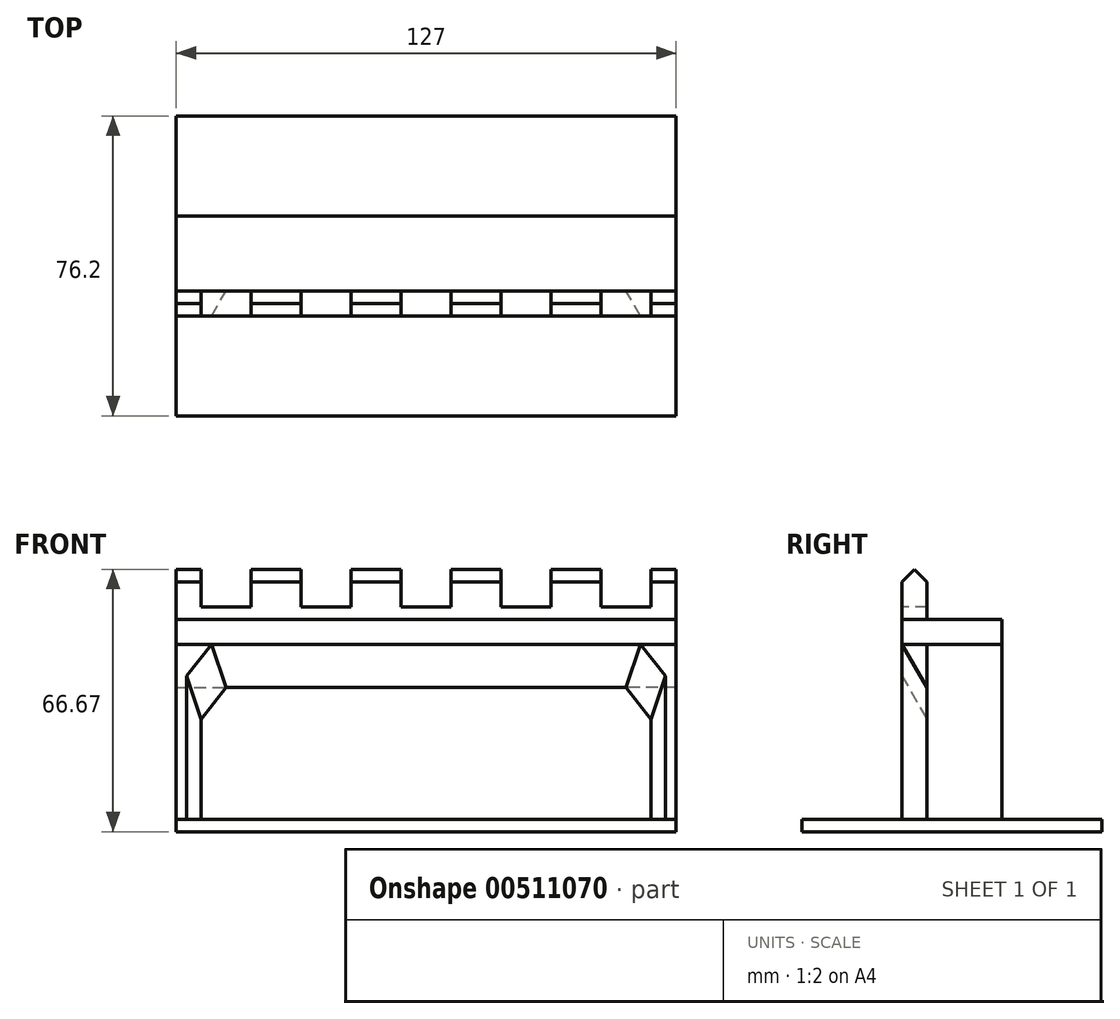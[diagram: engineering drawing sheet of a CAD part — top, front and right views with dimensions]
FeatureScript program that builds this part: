
annotation { "Feature Type Name" : "Feature", "Feature Type Description" : "" }
export const myFeature = defineFeature(function(context is Context, id is Id, definition is map)
    precondition{}
    {
        {
            var Q0;
            Q0=qCreatedBy(makeId("Top.planeOp"),FACE);
            var sketch = newSketch(context, id + "F0", { "sketchPlane" : qUnion([Q0])});
            skLineSegment(sketch, "E0.bottom", {"start": v(63.5, 38.1) * mm, "end": v(-63.5, 38.1) * mm});
            skLineSegment(sketch, "E0.top", {"start": v(63.5, -38.1) * mm, "end": v(-63.5, -38.1) * mm});
            skLineSegment(sketch, "E0.left", {"start": v(63.5, 38.1) * mm, "end": v(63.5, -38.1) * mm});
            skLineSegment(sketch, "E0.right", {"start": v(-63.5, 38.1) * mm, "end": v(-63.5, -38.1) * mm});
            skPoint(sketch, "E0.middle", {"position": v(0, 0) * mm});
            skSolve(sketch);
        }
        {
            var Q0;
            Q0 = qSketchRegion(id + "F0", true);
            extrude(context, id + "F1", {"entities" : qUnion([Q0]), "depth" : 3.17 * mm});
        }
        {
            var Q0;
            Q0=makeQuery(id+"F1.opExtrude","CAP_FACE",FACE,{"disambiguationData":[OSD([sQuery(id+"F0.wireOp",EDGE,"E0.bottom"),sQuery(id+"F0.wireOp",EDGE,"E0.top"),sQuery(id+"F0.wireOp",EDGE,"E0.left"),sQuery(id+"F0.wireOp",EDGE,"E0.right")])],"isStart":false});
            var sketch = newSketch(context, id + "F2", { "sketchPlane" : qUnion([Q0])});
            skLineSegment(sketch, "E1.bottom", {"start": v(-63.5, -6.35) * mm, "end": v(63.5, -6.35) * mm});
            skLineSegment(sketch, "E1.top", {"start": v(-63.5, 12.7) * mm, "end": v(63.5, 12.7) * mm});
            skLineSegment(sketch, "E1.left", {"start": v(-63.5, -6.35) * mm, "end": v(-63.5, 12.7) * mm});
            skLineSegment(sketch, "E1.right", {"start": v(63.5, -6.35) * mm, "end": v(63.5, 12.7) * mm});
            skSolve(sketch);
        }
        {
            var Q0;
            Q0 = qSketchRegion(id + "F2", true);
            extrude(context, id + "F3", {"entities" : qUnion([Q0]), "depth" : 44.45 * mm});
        }
        {
            var Q0;
            Q0=makeQuery(id+"F3.opExtrude","CAP_FACE",FACE,{"disambiguationData":[OSD([sQuery(id+"F2.wireOp",EDGE,"E1.bottom"),sQuery(id+"F2.wireOp",EDGE,"E1.top"),sQuery(id+"F2.wireOp",EDGE,"E1.left"),sQuery(id+"F2.wireOp",EDGE,"E1.right")])],"isStart":false});
            var sketch = newSketch(context, id + "F4", { "sketchPlane" : qUnion([Q0])});
            skLineSegment(sketch, "E2.bottom", {"start": v(-63.5, 12.7) * mm, "end": v(63.5, 12.7) * mm});
            skLineSegment(sketch, "E2.top", {"start": v(-63.5, -12.7) * mm, "end": v(63.5, -12.7) * mm});
            skLineSegment(sketch, "E2.left", {"start": v(-63.5, 12.7) * mm, "end": v(-63.5, -12.7) * mm});
            skLineSegment(sketch, "E2.right", {"start": v(63.5, 12.7) * mm, "end": v(63.5, -12.7) * mm});
            skSolve(sketch);
        }
        {
            var Q0;
            {var subQ0=sQuery(id+"F4.wireOp",EDGE,"E2.top");Q0=makeQuery(id+"F4.imprint","IMPRINT",FACE,{"disambiguationData":[TD([[makeQuery(id+"F4.imprint","IMPRINT",EDGE,{"derivedFrom":subQ0}),1.0]])]});}
            var Q1;
            {var subQ0=sQuery(id+"F4.wireOp",EDGE,"E2.bottom");Q1=makeQuery(id+"F4.imprint","IMPRINT",FACE,{"disambiguationData":[TD([[makeQuery(id+"F4.imprint","IMPRINT",EDGE,{"derivedFrom":subQ0}),-1.0]])]});}
            extrude(context, id + "F5", {"entities" : qUnion([Q0, Q1]), "depth" : 6.35 * mm});
        }
        {
            var Q0;
            Q0=makeQuery(id+"F5.opExtrude","CAP_FACE",FACE,{"disambiguationData":[OSD([sQuery(id+"F4.wireOp",EDGE,"E2.bottom"),sQuery(id+"F4.wireOp",EDGE,"E2.top"),sQuery(id+"F4.wireOp",EDGE,"E2.left"),sQuery(id+"F4.wireOp",EDGE,"E2.right")])],"isStart":false});
            var sketch = newSketch(context, id + "F6", { "sketchPlane" : qUnion([Q0])});
            skLineSegment(sketch, "E3.bottom", {"start": v(-63.5, -12.7) * mm, "end": v(63.5, -12.7) * mm});
            skLineSegment(sketch, "E3.top", {"start": v(-63.5, -6.35) * mm, "end": v(63.5, -6.35) * mm});
            skLineSegment(sketch, "E3.left", {"start": v(-63.5, -12.7) * mm, "end": v(-63.5, -6.35) * mm});
            skLineSegment(sketch, "E3.right", {"start": v(63.5, -12.7) * mm, "end": v(63.5, -6.35) * mm});
            skSolve(sketch);
        }
        {
            var Q0;
            Q0 = qSketchRegion(id + "F6", true);
            extrude(context, id + "F7", {"entities" : qUnion([Q0]), "depth" : 12.7 * mm});
        }
        {
            var Q0;
            Q0=makeQuery(id+"F7.opExtrude","SWEPT_FACE",FACE,{"disambiguationData":[OSD([sQuery(id+"F6.wireOp",EDGE,"E3.right")])]});
            var sketch = newSketch(context, id + "F8", { "sketchPlane" : qUnion([Q0])});
            skLineSegment(sketch, "E4.bottom", {"start": v(-12.7, 66.67) * mm, "end": v(-6.35, 66.67) * mm});
            skLineSegment(sketch, "E4.top", {"start": v(-12.7, 63.5) * mm, "end": v(-6.35, 63.5) * mm, "construction": true});
            skLineSegment(sketch, "E4.left", {"start": v(-12.7, 66.67) * mm, "end": v(-12.7, 63.5) * mm});
            skLineSegment(sketch, "E4.right", {"start": v(-6.35, 66.67) * mm, "end": v(-6.35, 63.5) * mm});
            skLineSegment(sketch, "E5", {"start": v(-12.7, 63.5) * mm, "end": v(-9.52, 66.67) * mm});
            skLineSegment(sketch, "E6", {"start": v(-9.53, 66.67) * mm, "end": v(-6.35, 63.5) * mm});
            skSolve(sketch);
        }
        {
            var Q0;
            Q0 = qSketchRegion(id + "F8", true);
            var Q1;
            Q1=makeQuery(id+"F7.opExtrude","SWEPT_FACE",FACE,{"disambiguationData":[OSD([sQuery(id+"F6.wireOp",EDGE,"E3.left")])]});
            extrude(context, id + "F9", {"entities" : qUnion([Q0]), "operationType" : NewBodyOperationType.REMOVE, "endBound" : BoundingType.UP_TO_SURFACE, "oppositeDirection" : true, "endBoundEntityFace" : qUnion([Q1]), "depth" : 25.4 * mm});
        }
        {
            var Q0;
            Q0=makeQuery(id+"F7.opExtrude","SWEPT_FACE",FACE,{"disambiguationData":[OSD([sQuery(id+"F6.wireOp",EDGE,"E3.bottom")])]});
            var sketch = newSketch(context, id + "F10", { "sketchPlane" : qUnion([Q0])});
            skLineSegment(sketch, "E7.bottom", {"start": v(-57.15, 66.67) * mm, "end": v(-44.45, 66.67) * mm});
            skLineSegment(sketch, "E7.top", {"start": v(-57.15, 57.15) * mm, "end": v(-44.45, 57.15) * mm});
            skLineSegment(sketch, "E7.left", {"start": v(-57.15, 66.67) * mm, "end": v(-57.15, 57.15) * mm});
            skLineSegment(sketch, "E7.right", {"start": v(-44.45, 66.67) * mm, "end": v(-44.45, 57.15) * mm});
            skLineSegment(sketch, "E8", {"start": v(-44.45, 61.91) * mm, "end": v(-31.75, 61.91) * mm, "construction": true});
            skLineSegment(sketch, "E9.bottom", {"start": v(-31.75, 66.67) * mm, "end": v(-19.05, 66.67) * mm});
            skLineSegment(sketch, "E9.top", {"start": v(-31.75, 57.15) * mm, "end": v(-19.05, 57.15) * mm});
            skLineSegment(sketch, "E9.left", {"start": v(-31.75, 66.67) * mm, "end": v(-31.75, 57.15) * mm});
            skLineSegment(sketch, "E9.right", {"start": v(-19.05, 66.67) * mm, "end": v(-19.05, 57.15) * mm});
            skLineSegment(sketch, "E10", {"start": v(-19.05, 61.91) * mm, "end": v(-6.35, 61.91) * mm, "construction": true});
            skLineSegment(sketch, "E11.bottom", {"start": v(-6.35, 66.67) * mm, "end": v(0, 66.67) * mm});
            skLineSegment(sketch, "E11.top", {"start": v(-6.35, 57.15) * mm, "end": v(0, 57.15) * mm});
            skLineSegment(sketch, "E11.left", {"start": v(-6.35, 66.67) * mm, "end": v(-6.35, 57.15) * mm});
            skLineSegment(sketch, "E12.MirrorCS", {"start": v(6.35, 66.67) * mm, "end": v(6.35, 57.15) * mm});
            skLineSegment(sketch, "E13.MirrorCS", {"start": v(19.05, 61.91) * mm, "end": v(6.35, 61.91) * mm, "construction": true});
            skLineSegment(sketch, "E14.MirrorCS", {"start": v(6.35, 66.67) * mm, "end": v(0, 66.67) * mm});
            skLineSegment(sketch, "E15.MirrorCS", {"start": v(19.05, 66.67) * mm, "end": v(19.05, 57.15) * mm});
            skLineSegment(sketch, "E16.MirrorCS", {"start": v(44.45, 66.67) * mm, "end": v(44.45, 57.15) * mm});
            skLineSegment(sketch, "E17.MirrorCS", {"start": v(6.35, 57.15) * mm, "end": v(0, 57.15) * mm});
            skLineSegment(sketch, "E18.MirrorCS", {"start": v(57.15, 66.67) * mm, "end": v(57.15, 57.15) * mm});
            skLineSegment(sketch, "E19.MirrorCS", {"start": v(57.15, 57.15) * mm, "end": v(44.45, 57.15) * mm});
            skLineSegment(sketch, "E20.MirrorCS", {"start": v(57.15, 66.67) * mm, "end": v(44.45, 66.67) * mm});
            skLineSegment(sketch, "E21.MirrorCS", {"start": v(31.75, 57.15) * mm, "end": v(19.05, 57.15) * mm});
            skLineSegment(sketch, "E22.MirrorCS", {"start": v(31.75, 66.67) * mm, "end": v(19.05, 66.67) * mm});
            skLineSegment(sketch, "E23.MirrorCS", {"start": v(44.45, 61.91) * mm, "end": v(31.75, 61.91) * mm, "construction": true});
            skLineSegment(sketch, "E24.MirrorCS", {"start": v(31.75, 66.67) * mm, "end": v(31.75, 57.15) * mm});
            skSolve(sketch);
        }
        {
            var Q0;
            Q0 = qSketchRegion(id + "F10", true);
            var Q1;
            Q1=makeQuery(id+"F7.opExtrude","SWEPT_FACE",FACE,{"disambiguationData":[OSD([sQuery(id+"F6.wireOp",EDGE,"E3.top")])]});
            extrude(context, id + "F11", {"entities" : qUnion([Q0]), "operationType" : NewBodyOperationType.REMOVE, "endBound" : BoundingType.UP_TO_SURFACE, "oppositeDirection" : true, "endBoundEntityFace" : qUnion([Q1]), "depth" : 25.4 * mm});
        }
        {
            var Q0;
            Q0=makeQuery(id+"F3.opExtrude","SWEPT_FACE",FACE,{"disambiguationData":[OSD([sQuery(id+"F2.wireOp",EDGE,"E1.right")])]});
            var sketch = newSketch(context, id + "F12", { "sketchPlane" : qUnion([Q0])});
            skLineSegment(sketch, "E25", {"start": v(-12.7, 47.62) * mm, "end": v(-6.35, 36.63) * mm});
            skLineSegment(sketch, "E26", {"start": v(-6.35, 47.62) * mm, "end": v(-6.35, 36.63) * mm});
            skLineSegment(sketch, "E27", {"start": v(-6.35, 47.62) * mm, "end": v(-12.7, 47.62) * mm});
            skSolve(sketch);
        }
        {
            var Q0;
            Q0 = qSketchRegion(id + "F12", true);
            var Q1;
            Q1=makeQuery(id+"F3.opExtrude","SWEPT_FACE",FACE,{"disambiguationData":[OSD([sQuery(id+"F2.wireOp",EDGE,"E1.left")])]});
            extrude(context, id + "F13", {"entities" : qUnion([Q0]), "endBound" : BoundingType.UP_TO_SURFACE, "oppositeDirection" : true, "endBoundEntityFace" : qUnion([Q1]), "depth" : 25.4 * mm});
        }
        {
            var Q0;
            Q0=makeQuery(id+"F1.opExtrude","CAP_FACE",FACE,{"disambiguationData":[OSD([sQuery(id+"F0.wireOp",EDGE,"E0.bottom"),sQuery(id+"F0.wireOp",EDGE,"E0.top"),sQuery(id+"F0.wireOp",EDGE,"E0.left"),sQuery(id+"F0.wireOp",EDGE,"E0.right")])],"isStart":false});
            var sketch = newSketch(context, id + "F14", { "sketchPlane" : qUnion([Q0])});
            skLineSegment(sketch, "E28.bottom", {"start": v(50.8, -6.35) * mm, "end": v(63.5, -6.35) * mm});
            skLineSegment(sketch, "E28.top", {"start": v(54.47, -12.7) * mm, "end": v(63.5, -12.7) * mm});
            skLineSegment(sketch, "E28.left", {"start": v(50.8, -6.35) * mm, "end": v(54.47, -12.7) * mm});
            skLineSegment(sketch, "E28.right", {"start": v(76.2, -6.35) * mm, "end": v(72.53, -12.7) * mm, "construction": true});
            skLineSegment(sketch, "E29", {"start": v(63.5, -6.35) * mm, "end": v(63.5, -12.7) * mm});
            skLineSegment(sketch, "E30", {"start": v(63.5, -12.7) * mm, "end": v(72.53, -12.7) * mm, "construction": true});
            skLineSegment(sketch, "E31", {"start": v(63.5, -6.35) * mm, "end": v(76.2, -6.35) * mm, "construction": true});
            skSolve(sketch);
        }
        {
            var Q0;
            Q0 = qSketchRegion(id + "F14", true);
            var Q1;
            Q1=makeQuery(id+"F13.opExtrude","SWEPT_FACE",FACE,{"disambiguationData":[OSD([sQuery(id+"F12.wireOp",EDGE,"E25")])]});
            extrude(context, id + "F15", {"entities" : qUnion([Q0]), "endBound" : BoundingType.UP_TO_SURFACE, "endBoundEntityFace" : qUnion([Q1]), "depth" : 25.4 * mm});
        }
        {
            var Q0;
            Q0=makeQuery(id+"F1.opExtrude","CAP_FACE",FACE,{"disambiguationData":[OSD([sQuery(id+"F0.wireOp",EDGE,"E0.bottom"),sQuery(id+"F0.wireOp",EDGE,"E0.top"),sQuery(id+"F0.wireOp",EDGE,"E0.left"),sQuery(id+"F0.wireOp",EDGE,"E0.right")])],"isStart":false});
            var sketch = newSketch(context, id + "F16", { "sketchPlane" : qUnion([Q0])});
            skLineSegment(sketch, "E32.bottom", {"start": v(57.15, -6.35) * mm, "end": v(63.5, -6.35) * mm, "construction": true});
            skLineSegment(sketch, "E32.top", {"start": v(60.82, -12.7) * mm, "end": v(63.5, -12.7) * mm, "construction": true});
            skLineSegment(sketch, "E32.left", {"start": v(57.15, -6.35) * mm, "end": v(60.82, -12.7) * mm});
            skLineSegment(sketch, "E32.right", {"start": v(69.85, -6.35) * mm, "end": v(66.18, -12.7) * mm, "construction": true});
            skLineSegment(sketch, "E33", {"start": v(63.5, -6.35) * mm, "end": v(63.5, -12.7) * mm});
            skLineSegment(sketch, "E34", {"start": v(63.5, -12.7) * mm, "end": v(66.18, -12.7) * mm, "construction": true});
            skLineSegment(sketch, "E35", {"start": v(63.5, -6.35) * mm, "end": v(69.85, -6.35) * mm, "construction": true});
            skLineSegment(sketch, "E36", {"start": v(60.82, -12.7) * mm, "end": v(54.47, -12.7) * mm});
            skLineSegment(sketch, "E37", {"start": v(54.47, -12.7) * mm, "end": v(50.8, -6.35) * mm});
            skLineSegment(sketch, "E38", {"start": v(50.8, -6.35) * mm, "end": v(57.15, -6.35) * mm});
            skSolve(sketch);
        }
        {
            var Q0;
            Q0 = qSketchRegion(id + "F16", true);
            extrude(context, id + "F17", {"entities" : qUnion([Q0]), "operationType" : NewBodyOperationType.REMOVE, "depth" : 25.4 * mm});
        }
        {
            var Q0;
            Q0=makeQuery(id+"F15.opExtrude","CAP_VERTEX",VERTEX,{"disambiguationData":[OSD([sQuery(id+"F12.wireOp",EDGE,"E25"),sQuery(id+"F14.wireOp",EDGE,"E28.top"),sQuery(id+"F14.wireOp",EDGE,"E28.left")])],"isStart":false});
            var Q1;
            Q1=makeQuery(id+"F17.boolean.opBoolean","COPY",VERTEX,{"derivedFrom":makeQuery(id+"F17.opExtrude","CAP_VERTEX",VERTEX,{"disambiguationData":[OSD([sQuery(id+"F16.wireOp",EDGE,"E32.left"),sQuery(id+"F16.wireOp",EDGE,"E38")])],"isStart":false})});
            var Q2;
            Q2=makeQuery(id+"F15.opExtrude","CAP_VERTEX",VERTEX,{"disambiguationData":[OSD([sQuery(id+"F12.wireOp",EDGE,"E25"),sQuery(id+"F14.wireOp",EDGE,"E28.bottom"),sQuery(id+"F14.wireOp",EDGE,"E28.left")])],"isStart":false});
            cPlane(context, id + "F18", {"entities" : qUnion([Q0, Q1, Q2]), "cplaneType" : CPlaneType.THREE_POINT, "offset" : 25.4 * mm, "width" : 152.4 * mm, "height" : 152.4 * mm});
        }
        {
            var Q0;
            Q0=makeQuery(id+"F17.boolean.opBoolean","COPY",FACE,{"derivedFrom":makeQuery(id+"F17.opExtrude","CAP_FACE",FACE,{"disambiguationData":[OSD([sQuery(id+"F16.wireOp",EDGE,"E32.left"),sQuery(id+"F16.wireOp",EDGE,"E36"),sQuery(id+"F16.wireOp",EDGE,"E37"),sQuery(id+"F16.wireOp",EDGE,"E38")])],"isStart":false})});
            var Q1;
            Q1=qCreatedBy(id+"F18.planeOp",FACE);
            extrude(context, id + "F19", {"entities" : qUnion([Q0]), "operationType" : NewBodyOperationType.REMOVE, "endBound" : BoundingType.UP_TO_SURFACE, "oppositeDirection" : true, "endBoundEntityFace" : qUnion([Q1]), "depth" : 25.4 * mm});
        }
        {
            var Q0;
            Q0=makeQuery(id+"F15.opExtrude","SWEPT_BODY",BODY,{"disambiguationData":[OSD([sQuery(id+"F14.wireOp",EDGE,"E28.bottom"),sQuery(id+"F14.wireOp",EDGE,"E28.top"),sQuery(id+"F14.wireOp",EDGE,"E28.left"),sQuery(id+"F14.wireOp",EDGE,"E29")])]});
            var Q1;
            Q1=qCreatedBy(makeId("Right.planeOp"),FACE);
            mirror(context, id + "F20", {"entities" : qUnion([Q0]), "mirrorPlane" : qUnion([Q1])});
        }
    });
